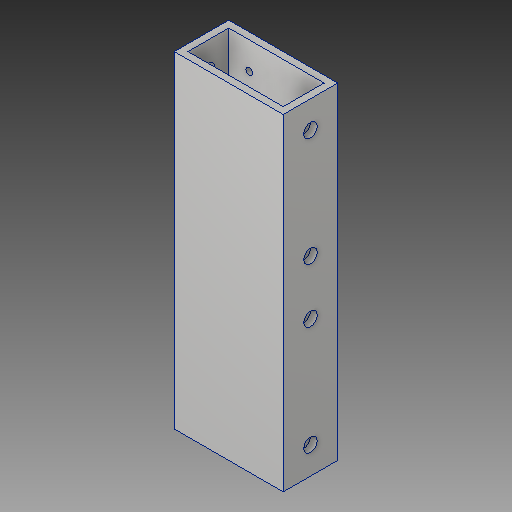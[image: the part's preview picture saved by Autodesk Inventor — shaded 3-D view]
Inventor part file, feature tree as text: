
AUTODESK INVENTOR PART (.ipt)
format: ipt  version: 2017 (Build 210142000, 142)  size: 138,240 bytes
history: native  units: in
note: dims shown in document units (in); Inventor stores cm internally (conversion verified against a paired STEP export)
features: sketch x3, hole x2, extrude x1
ambient origin geometry x8: Origin, YZ Plane, XZ Plane, XY Plane, X Axis, Y Axis, Z Axis, Center Point
bodies: Solid1 (feature_tree)
feature tree (6):
  extrude  "Extrusion1"  Depth=1.0in
  hole  "Hole2"  [1 undecoded]
  hole  "Hole3"  [1 undecoded]
  sketch  "Sketch1"  dims[d0=2.0in d1=1.0in]
  sketch  "Sketch2"  dims[d2=1.75in d3=0.75in]
  sketch  "Sketch3"  dims[d4=0.125in d5=0.125in d6=6.0in d7=0.0in d8=0.25in d9=0.5in d10=0.25in d11=0.5in d19=0.25in d20=0.75in d21=0.375in d22=0.25in d23=0.5635in d24=1.0in d25=0.8108in d27=0.5in d28=0.5in d30=0.125in d31=1.0in d32=0.125in d33=0.75in d34=0.375in d35=0.25in d36=0.5635in d37=0.125in d38=0.8108in]
note: 2 required parameter values undecoded (feature->parameter linkage not recoverable at this tier; creation-order binding heuristic only, values carry confidence <= 0.55)
